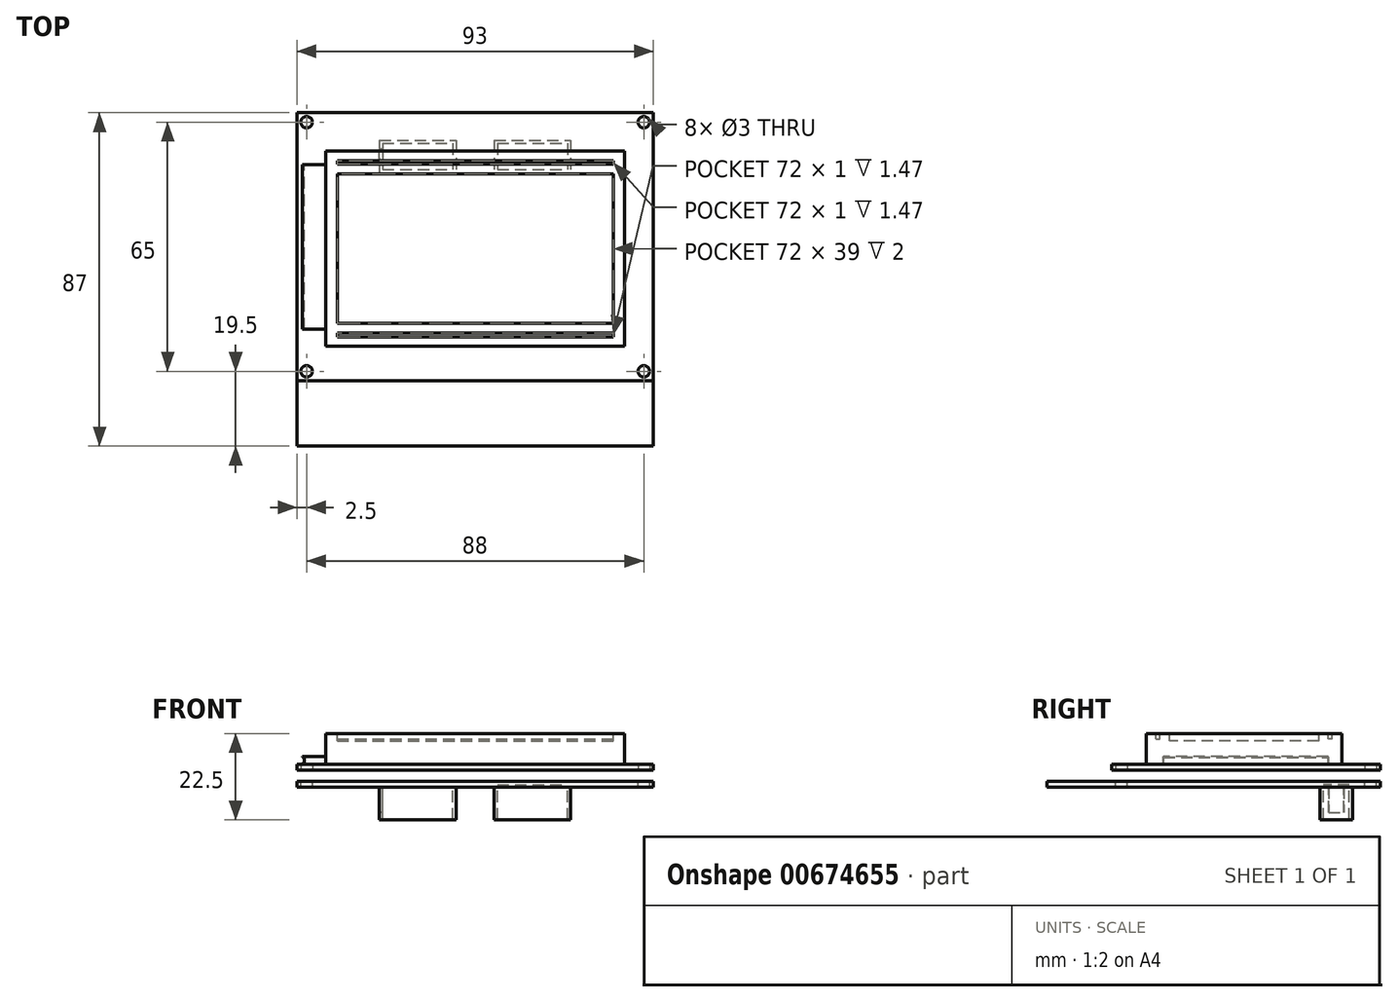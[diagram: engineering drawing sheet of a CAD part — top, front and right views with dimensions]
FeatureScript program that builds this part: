
annotation { "Feature Type Name" : "Feature", "Feature Type Description" : "" }
export const myFeature = defineFeature(function(context is Context, id is Id, definition is map)
    precondition{}
    {
        {
            var Q0;
            Q0=qCreatedBy(makeId("Top.planeOp"),FACE);
            var sketch = newSketch(context, id + "F0", { "sketchPlane" : qUnion([Q0])});
            skLineSegment(sketch, "E0.bottom", {"start": v(-46.5, 43.5) * mm, "end": v(46.5, 43.5) * mm});
            skLineSegment(sketch, "E0.top", {"start": v(-46.5, -43.5) * mm, "end": v(46.5, -43.5) * mm});
            skLineSegment(sketch, "E0.left", {"start": v(-46.5, 43.5) * mm, "end": v(-46.5, -43.5) * mm});
            skLineSegment(sketch, "E0.right", {"start": v(46.5, 43.5) * mm, "end": v(46.5, -43.5) * mm});
            skSolve(sketch);
        }
        {
            var Q0;
            Q0=makeQuery(id+"F0.imprint","IMPRINT",FACE,{"disambiguationData":[TD([[makeQuery(id+"F0.imprint","IMPRINT",EDGE,{"derivedFrom":sQuery(id+"F0.wireOp",EDGE,"E0.bottom")}),-1.0]])]});
            extrude(context, id + "F1", {"entities" : qUnion([Q0]), "depth" : 1.5 * mm, "offsetDistance" : 25 * mm});
        }
        {
            var Q0;
            Q0=makeQuery(id+"F1.opExtrude","CAP_FACE",FACE,{"disambiguationData":[OSD([sQuery(id+"F0.wireOp",EDGE,"E0.bottom"),sQuery(id+"F0.wireOp",EDGE,"E0.top"),sQuery(id+"F0.wireOp",EDGE,"E0.left"),sQuery(id+"F0.wireOp",EDGE,"E0.right")])],"isStart":false});
            var sketch = newSketch(context, id + "F2", { "sketchPlane" : qUnion([Q0])});
            skPoint(sketch, "E1", {"position": v(-44, 41) * mm});
            skPoint(sketch, "E2", {"position": v(44, 41) * mm});
            skPoint(sketch, "E3", {"position": v(44, -24) * mm});
            skPoint(sketch, "E4", {"position": v(-44, -24) * mm});
            skSolve(sketch);
        }
        {
            var Q0;
            Q0=sQuery(id+"F2.wireOp",VERTEX,"E1");
            var Q1;
            Q1=sQuery(id+"F2.wireOp",VERTEX,"E2");
            var Q2;
            Q2=sQuery(id+"F2.wireOp",VERTEX,"E3");
            var Q3;
            Q3=sQuery(id+"F2.wireOp",VERTEX,"E4");
            var Q4;
            Q4=makeQuery(id+"F1.opExtrude","SWEPT_BODY",BODY,{"disambiguationData":[OSD([sQuery(id+"F0.wireOp",EDGE,"E0.bottom"),sQuery(id+"F0.wireOp",EDGE,"E0.top"),sQuery(id+"F0.wireOp",EDGE,"E0.left"),sQuery(id+"F0.wireOp",EDGE,"E0.right")])]});
            hole(context, id + "F3", {"style" : HoleStyle.SIMPLE, "endStyle" : HoleEndStyle.THROUGH, "holeDiameter" : 3 * mm, "majorDiameter" : 5 * mm, "isTappedThrough" : true, "tappedDepth" : 12 * mm, "tapClearance" : 3, "startFromSketch" : true, "locations" : qUnion([Q0, Q1, Q2, Q3]), "scope" : qUnion([Q4])});
        }
        {
            var Q0;
            Q0=makeQuery(id+"F1.opExtrude","CAP_FACE",FACE,{"disambiguationData":[OSD([sQuery(id+"F0.wireOp",EDGE,"E0.bottom"),sQuery(id+"F0.wireOp",EDGE,"E0.top"),sQuery(id+"F0.wireOp",EDGE,"E0.left"),sQuery(id+"F0.wireOp",EDGE,"E0.right")])],"isStart":false});
            cPlane(context, id + "F4", {"entities" : qUnion([Q0]), "cplaneType" : CPlaneType.OFFSET, "offset" : 3 * mm, "width" : 150 * mm, "height" : 150 * mm});
        }
        {
            var Q0;
            Q0=qCreatedBy(id+"F4.planeOp",FACE);
            var sketch = newSketch(context, id + "F5", { "sketchPlane" : qUnion([Q0])});
            skLineSegment(sketch, "E5.0", {"start": v(-46.5, 43.5) * mm, "end": v(46.5, 43.5) * mm, "construction": true});
            skCircle(sketch, "E6.0", {"center": v(-44, 41) * mm, "radius": 1.5 * mm, "construction": true});
            skCircle(sketch, "E6.1", {"center": v(44, 41) * mm, "radius": 1.5 * mm, "construction": true});
            skCircle(sketch, "E6.2", {"center": v(44, -24) * mm, "radius": 1.5 * mm, "construction": true});
            skCircle(sketch, "E6.3", {"center": v(-44, -24) * mm, "radius": 1.5 * mm, "construction": true});
            skLineSegment(sketch, "E7.bottom", {"start": v(-46.5, 43.5) * mm, "end": v(46.5, 43.5) * mm});
            skLineSegment(sketch, "E7.top", {"start": v(-46.5, -26.5) * mm, "end": v(46.5, -26.5) * mm});
            skLineSegment(sketch, "E7.left", {"start": v(-46.5, 43.5) * mm, "end": v(-46.5, -26.5) * mm});
            skLineSegment(sketch, "E7.right", {"start": v(46.5, 43.5) * mm, "end": v(46.5, -26.5) * mm});
            skSolve(sketch);
        }
        {
            var Q0;
            Q0=makeQuery(id+"F5.imprint","IMPRINT",FACE,{"disambiguationData":[TD([[makeQuery(id+"F5.imprint","IMPRINT",EDGE,{"derivedFrom":sQuery(id+"F5.wireOp",EDGE,"E7.bottom")}),-1.0]])]});
            extrude(context, id + "F6", {"entities" : qUnion([Q0]), "depth" : 1.5 * mm, "offsetDistance" : 25 * mm});
        }
        {
            var Q0;
            Q0=sQuery(id+"F5.wireOp",VERTEX,"E6.0.center");
            var Q1;
            Q1=sQuery(id+"F5.wireOp",VERTEX,"E6.1.center");
            var Q2;
            Q2=sQuery(id+"F5.wireOp",VERTEX,"E6.2.center");
            var Q3;
            Q3=sQuery(id+"F5.wireOp",VERTEX,"E6.3.center");
            var Q4;
            Q4=makeQuery(id+"F6.opExtrude","SWEPT_BODY",BODY,{"disambiguationData":[OSD([sQuery(id+"F5.wireOp",EDGE,"E7.bottom"),sQuery(id+"F5.wireOp",EDGE,"E7.top"),sQuery(id+"F5.wireOp",EDGE,"E7.left"),sQuery(id+"F5.wireOp",EDGE,"E7.right")])]});
            hole(context, id + "F7", {"style" : HoleStyle.SIMPLE, "endStyle" : HoleEndStyle.THROUGH, "oppositeDirection" : true, "holeDiameter" : 3 * mm, "majorDiameter" : 5 * mm, "isTappedThrough" : true, "tappedDepth" : 12 * mm, "tapClearance" : 3, "startFromSketch" : true, "locations" : qUnion([Q0, Q1, Q2, Q3]), "scope" : qUnion([Q4])});
        }
        {
            var Q0;
            Q0=makeQuery(id+"F6.opExtrude","CAP_FACE",FACE,{"disambiguationData":[OSD([sQuery(id+"F5.wireOp",EDGE,"E7.bottom"),sQuery(id+"F5.wireOp",EDGE,"E7.top"),sQuery(id+"F5.wireOp",EDGE,"E7.left"),sQuery(id+"F5.wireOp",EDGE,"E7.right")])],"isStart":false});
            var sketch = newSketch(context, id + "F8", { "sketchPlane" : qUnion([Q0])});
            skLineSegment(sketch, "E8.0", {"start": v(-46.5, -26.5) * mm, "end": v(46.5, -26.5) * mm, "construction": true});
            skLineSegment(sketch, "E8.1", {"start": v(-46.5, 43.5) * mm, "end": v(46.5, 43.5) * mm, "construction": true});
            skLineSegment(sketch, "E8.2", {"start": v(-46.5, 43.5) * mm, "end": v(-46.5, -26.5) * mm, "construction": true});
            skLineSegment(sketch, "E8.3", {"start": v(46.5, 43.5) * mm, "end": v(46.5, -26.5) * mm, "construction": true});
            skLineSegment(sketch, "E9.bottom", {"start": v(-39, 33.5) * mm, "end": v(39, 33.5) * mm});
            skLineSegment(sketch, "E9.top", {"start": v(-39, -17.5) * mm, "end": v(39, -17.5) * mm});
            skLineSegment(sketch, "E9.left", {"start": v(-39, 33.5) * mm, "end": v(-39, -17.5) * mm});
            skLineSegment(sketch, "E9.right", {"start": v(39, 33.5) * mm, "end": v(39, -17.5) * mm});
            skSolve(sketch);
        }
        {
            var Q0;
            Q0=makeQuery(id+"F8.imprint","IMPRINT",FACE,{"disambiguationData":[TD([[makeQuery(id+"F8.imprint","IMPRINT",EDGE,{"derivedFrom":sQuery(id+"F8.wireOp",EDGE,"E9.bottom")}),-1.0]])]});
            extrude(context, id + "F9", {"entities" : qUnion([Q0]), "depth" : 8 * mm, "offsetDistance" : 25 * mm});
        }
        {
            var Q0;
            Q0=makeQuery(id+"F9.opExtrude","CAP_FACE",FACE,{"disambiguationData":[OSD([sQuery(id+"F8.wireOp",EDGE,"E9.bottom"),sQuery(id+"F8.wireOp",EDGE,"E9.top"),sQuery(id+"F8.wireOp",EDGE,"E9.left"),sQuery(id+"F8.wireOp",EDGE,"E9.right")])],"isStart":false});
            var sketch = newSketch(context, id + "F10", { "sketchPlane" : qUnion([Q0])});
            skLineSegment(sketch, "E10.bottom", {"start": v(-36, -15) * mm, "end": v(36, -15) * mm});
            skLineSegment(sketch, "E10.top", {"start": v(-36, -14) * mm, "end": v(36, -14) * mm});
            skLineSegment(sketch, "E10.left", {"start": v(-36, -15) * mm, "end": v(-36, -14) * mm});
            skLineSegment(sketch, "E10.right", {"start": v(36, -15) * mm, "end": v(36, -14) * mm});
            skLineSegment(sketch, "E11", {"start": v(-59.63, 8) * mm, "end": v(-29.69, 8) * mm, "construction": true});
            skPoint(sketch, "E11.startSnap0", {"position": v(-39, 8) * mm});
            skLineSegment(sketch, "E12.MirrorCS", {"start": v(-36, 31) * mm, "end": v(-36, 30) * mm});
            skLineSegment(sketch, "E13.MirrorCS", {"start": v(36, 31) * mm, "end": v(36, 30) * mm});
            skLineSegment(sketch, "E14.MirrorCS", {"start": v(-36, 30) * mm, "end": v(36, 30) * mm});
            skLineSegment(sketch, "E15.MirrorCS", {"start": v(-36, 31) * mm, "end": v(36, 31) * mm});
            skLineSegment(sketch, "E16.bottom", {"start": v(-36, 27.5) * mm, "end": v(36, 27.5) * mm});
            skLineSegment(sketch, "E16.top", {"start": v(-36, -11.5) * mm, "end": v(36, -11.5) * mm});
            skLineSegment(sketch, "E16.left", {"start": v(-36, 27.5) * mm, "end": v(-36, -11.5) * mm});
            skLineSegment(sketch, "E16.right", {"start": v(36, 27.5) * mm, "end": v(36, -11.5) * mm});
            skSolve(sketch);
        }
        {
            var Q0;
            Q0=makeQuery(id+"F10.imprint","IMPRINT",FACE,{"disambiguationData":[TD([[makeQuery(id+"F10.imprint","IMPRINT",EDGE,{"derivedFrom":sQuery(id+"F10.wireOp",EDGE,"E12.MirrorCS")}),1.0]])]});
            var Q1;
            Q1=makeQuery(id+"F10.imprint","IMPRINT",FACE,{"disambiguationData":[TD([[makeQuery(id+"F10.imprint","IMPRINT",EDGE,{"derivedFrom":sQuery(id+"F10.wireOp",EDGE,"E10.bottom")}),1.0]])]});
            extrude(context, id + "F11", {"entities" : qUnion([Q0, Q1]), "operationType" : NewBodyOperationType.REMOVE, "oppositeDirection" : true, "depth" : 1.47 * mm, "offsetDistance" : 25 * mm});
        }
        {
            var Q0;
            Q0=makeQuery(id+"F10.imprint","IMPRINT",FACE,{"disambiguationData":[TD([[makeQuery(id+"F10.imprint","IMPRINT",EDGE,{"derivedFrom":sQuery(id+"F10.wireOp",EDGE,"E16.bottom")}),-1.0]])]});
            extrude(context, id + "F12", {"entities" : qUnion([Q0]), "operationType" : NewBodyOperationType.REMOVE, "oppositeDirection" : true, "depth" : 2 * mm, "offsetDistance" : 25 * mm});
        }
        {
            var Q0;
            Q0=makeQuery(id+"F9.opExtrude","SWEPT_FACE",FACE,{"disambiguationData":[OSD([sQuery(id+"F8.wireOp",EDGE,"E9.left")])]});
            var sketch = newSketch(context, id + "F13", { "sketchPlane" : qUnion([Q0])});
            skLineSegment(sketch, "E17.0", {"start": v(-43.5, 6) * mm, "end": v(26.5, 6) * mm, "construction": true});
            skLineSegment(sketch, "E18.bottom", {"start": v(-29.95, 6) * mm, "end": v(13.05, 6) * mm});
            skLineSegment(sketch, "E18.top", {"start": v(-29.95, 8) * mm, "end": v(13.05, 8) * mm});
            skLineSegment(sketch, "E18.left", {"start": v(-29.95, 6) * mm, "end": v(-29.95, 8) * mm});
            skLineSegment(sketch, "E18.right", {"start": v(13.05, 6) * mm, "end": v(13.05, 8) * mm});
            skSolve(sketch);
        }
        {
            var Q0;
            Q0=makeQuery(id+"F13.imprint","IMPRINT",FACE,{"disambiguationData":[TD([[makeQuery(id+"F13.imprint","IMPRINT",EDGE,{"derivedFrom":sQuery(id+"F13.wireOp",EDGE,"E18.bottom")}),1.0]])]});
            extrude(context, id + "F14", {"entities" : qUnion([Q0]), "depth" : 6.14 * mm, "offsetDistance" : 25 * mm});
        }
        {
            var Q0;
            Q0=makeQuery(id+"F14.opExtrude","SWEPT_FACE",FACE,{"disambiguationData":[OSD([sQuery(id+"F13.wireOp",EDGE,"E18.left")])]});
            var sketch = newSketch(context, id + "F15", { "sketchPlane" : qUnion([Q0])});
            skLineSegment(sketch, "E19.0", {"start": v(45.14, 8) * mm, "end": v(39, 8) * mm, "construction": true});
            skLineSegment(sketch, "E19.1", {"start": v(45.14, 6) * mm, "end": v(45.14, 8) * mm, "construction": true});
            skLineSegment(sketch, "E19.2", {"start": v(46.5, 6) * mm, "end": v(-46.5, 6) * mm, "construction": true});
            skLineSegment(sketch, "E20", {"start": v(45.14, 7.84) * mm, "end": v(44.64, 7.8) * mm});
            skLineSegment(sketch, "E21", {"start": v(44.64, 7.8) * mm, "end": v(44.64, 6.21) * mm});
            skLineSegment(sketch, "E22", {"start": v(44.64, 6.21) * mm, "end": v(45.14, 6.16) * mm});
            skLineSegment(sketch, "E23", {"start": v(45.14, 6.16) * mm, "end": v(45.14, 7.84) * mm});
            skLineSegment(sketch, "E24", {"start": v(45.7, 7) * mm, "end": v(44.78, 7) * mm, "construction": true});
            skPoint(sketch, "E24.startSnap0", {"position": v(45.14, 7) * mm});
            skSolve(sketch);
        }
        {
            var Q0;
            Q0=makeQuery(id+"F15.imprint","IMPRINT",FACE,{"disambiguationData":[TD([[makeQuery(id+"F15.imprint","IMPRINT",EDGE,{"derivedFrom":sQuery(id+"F15.wireOp",EDGE,"E20")}),1.0]])]});
            extrude(context, id + "F16", {"entities" : qUnion([Q0]), "operationType" : NewBodyOperationType.REMOVE, "endBound" : BoundingType.THROUGH_ALL, "oppositeDirection" : true, "depth" : 25 * mm, "offsetDistance" : 25 * mm});
        }
        {
            var Q0;
            Q0=makeQuery(id+"F1.opExtrude","CAP_FACE",FACE,{"disambiguationData":[OSD([sQuery(id+"F0.wireOp",EDGE,"E0.bottom"),sQuery(id+"F0.wireOp",EDGE,"E0.top"),sQuery(id+"F0.wireOp",EDGE,"E0.left"),sQuery(id+"F0.wireOp",EDGE,"E0.right")])],"isStart":true});
            var sketch = newSketch(context, id + "F17", { "sketchPlane" : qUnion([Q0])});
            skLineSegment(sketch, "E25.bottom", {"start": v(-25, -36.3) * mm, "end": v(-5, -36.3) * mm});
            skLineSegment(sketch, "E25.top", {"start": v(-25, -27.8) * mm, "end": v(-5, -27.8) * mm});
            skLineSegment(sketch, "E25.left", {"start": v(-25, -36.3) * mm, "end": v(-25, -27.8) * mm});
            skLineSegment(sketch, "E25.right", {"start": v(-5, -36.3) * mm, "end": v(-5, -27.8) * mm});
            skLineSegment(sketch, "E26.bottom", {"start": v(4.92, -36.3) * mm, "end": v(24.92, -36.3) * mm});
            skLineSegment(sketch, "E26.top", {"start": v(4.92, -27.8) * mm, "end": v(24.92, -27.8) * mm});
            skLineSegment(sketch, "E26.left", {"start": v(4.92, -36.3) * mm, "end": v(4.92, -27.8) * mm});
            skLineSegment(sketch, "E26.right", {"start": v(24.92, -36.3) * mm, "end": v(24.92, -27.8) * mm});
            skSolve(sketch);
        }
        {
            var Q0;
            Q0 = qSketchRegion(id + "F17", true);
            extrude(context, id + "F18", {"entities" : qUnion([Q0]), "operationType" : NewBodyOperationType.ADD, "depth" : 8.5 * mm, "offsetDistance" : 25 * mm});
        }
        {
            var Q0;
            Q0=makeQuery(id+"F18.opExtrude","CAP_FACE",FACE,{"disambiguationData":[OSD([sQuery(id+"F17.wireOp",EDGE,"E26.bottom"),sQuery(id+"F17.wireOp",EDGE,"E26.top"),sQuery(id+"F17.wireOp",EDGE,"E26.left"),sQuery(id+"F17.wireOp",EDGE,"E26.right")])],"isStart":false});
            var Q1;
            Q1=makeQuery(id+"F18.opExtrude","CAP_FACE",FACE,{"disambiguationData":[OSD([sQuery(id+"F17.wireOp",EDGE,"E25.bottom"),sQuery(id+"F17.wireOp",EDGE,"E25.top"),sQuery(id+"F17.wireOp",EDGE,"E25.left"),sQuery(id+"F17.wireOp",EDGE,"E25.right")])],"isStart":false});
            shell(context, id + "F19", {"entities" : qUnion([Q0, Q1]), "thickness" : 0.83 * mm});
        }
        {
            var Q0;
            Q0=makeQuery(id+"F18.opExtrude","SWEPT_FACE",FACE,{"disambiguationData":[OSD([sQuery(id+"F17.wireOp",EDGE,"E25.left")])]});
            var sketch = newSketch(context, id + "F20", { "sketchPlane" : qUnion([Q0])});
            skLineSegment(sketch, "E27.bottom", {"start": v(-30.05, 0) * mm, "end": v(-34.05, 0) * mm});
            skLineSegment(sketch, "E27.top", {"start": v(-30.05, -6.6) * mm, "end": v(-34.05, -6.6) * mm});
            skLineSegment(sketch, "E27.left", {"start": v(-30.05, 0) * mm, "end": v(-30.05, -6.6) * mm});
            skLineSegment(sketch, "E27.right", {"start": v(-34.05, 0) * mm, "end": v(-34.05, -6.6) * mm});
            skLineSegment(sketch, "E28", {"start": v(-32.05, -10.02) * mm, "end": v(-32.05, -5.62) * mm, "construction": true});
            skPoint(sketch, "E28.startSnap0", {"position": v(-32.05, -8.5) * mm});
            skSolve(sketch);
        }
        {
            var Q0;
            Q0=makeQuery(id+"F20.imprint","IMPRINT",FACE,{"disambiguationData":[TD([[makeQuery(id+"F20.imprint","IMPRINT",EDGE,{"derivedFrom":sQuery(id+"F20.wireOp",EDGE,"E27.bottom")}),-1.0]])]});
            var Q1;
            Q1=makeQuery(id+"F19.opShell","OFFSET_FACE",FACE,{"disambiguationData":[OSD([sQuery(id+"F17.wireOp",EDGE,"E25.left")])]});
            extrude(context, id + "F21", {"entities" : qUnion([Q0]), "operationType" : NewBodyOperationType.REMOVE, "endBound" : BoundingType.UP_TO_SURFACE, "oppositeDirection" : true, "depth" : 25 * mm, "endBoundEntityFace" : qUnion([Q1]), "offsetDistance" : 25 * mm});
        }
        {
            var Q0;
            Q0=makeQuery(id+"F19.opShell","OFFSET_FACE",FACE,{"disambiguationData":[OSD([sQuery(id+"F0.wireOp",EDGE,"E0.bottom"),sQuery(id+"F0.wireOp",EDGE,"E0.top"),sQuery(id+"F0.wireOp",EDGE,"E0.left"),sQuery(id+"F0.wireOp",EDGE,"E0.right")]),OD(0.0)]});
            extrude(context, id + "F22", {"entities" : qUnion([Q0]), "operationType" : NewBodyOperationType.ADD, "depth" : 0.83 * mm, "offsetDistance" : 25 * mm});
        }
    });
